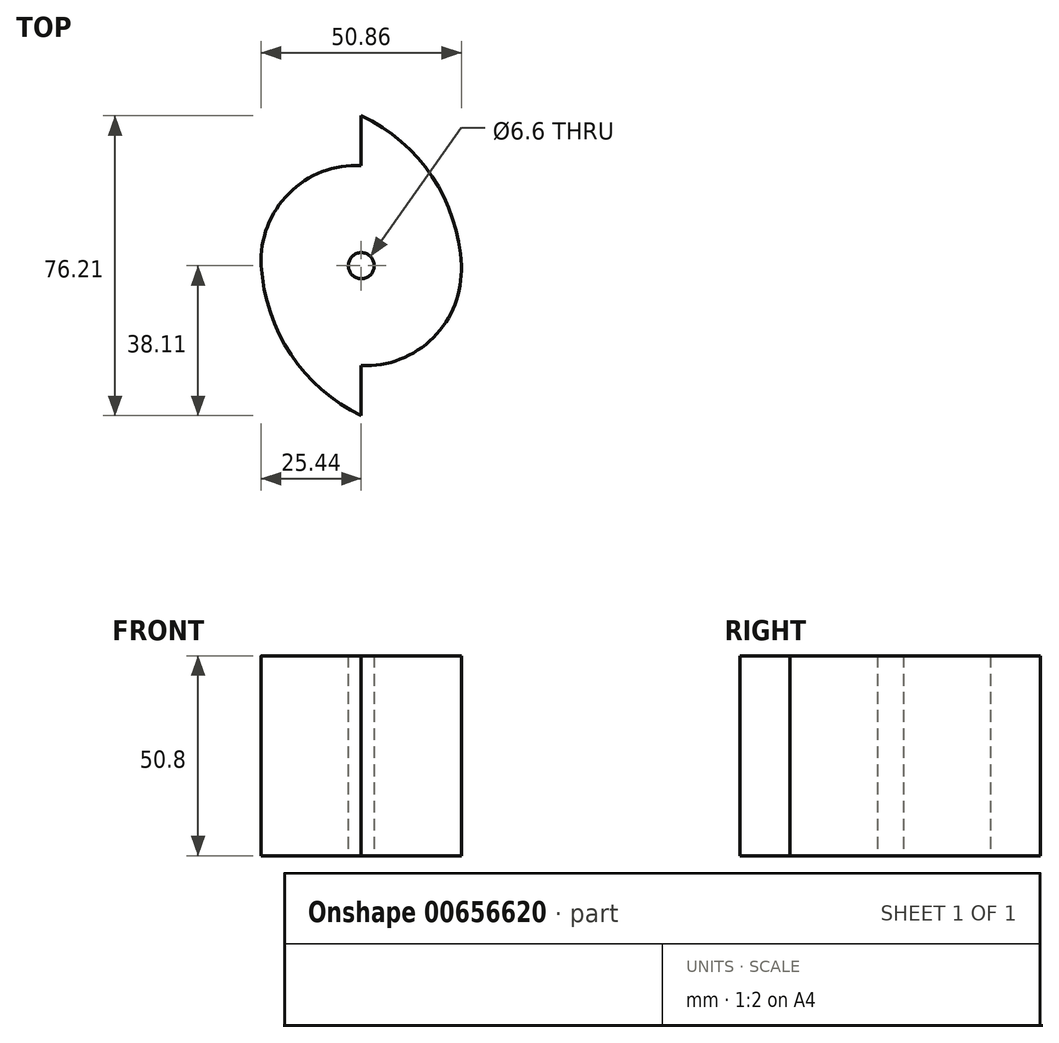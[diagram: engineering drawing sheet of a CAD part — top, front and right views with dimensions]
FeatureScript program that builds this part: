
annotation { "Feature Type Name" : "Feature", "Feature Type Description" : "" }
export const myFeature = defineFeature(function(context is Context, id is Id, definition is map)
    precondition{}
    {
        {
            var Q0;
            Q0=qCreatedBy(makeId("Top.planeOp"),FACE);
            var sketch = newSketch(context, id + "F0", { "sketchPlane" : qUnion([Q0])});
            skCircle(sketch, "E0", {"center": v(0, 0) * mm, "radius": 3.3 * mm});
            skLineSegment(sketch, "E1", {"start": v(0, 25.4) * mm, "end": v(0, 38.1) * mm});
            skLineSegment(sketch, "E2", {"start": v(0, -25.4) * mm, "end": v(0, -38.11) * mm});
            skArc(sketch, "E3", {"start": v(25.4, 0) * mm, "mid": v(18.02, 22.6) * mm, "end": v(0, 38.1) * mm});
            skArc(sketch, "E4", {"start": v(-25.4, 0) * mm, "mid": v(-17.89, -22.51) * mm, "end": v(0, -38.11) * mm});
            skArc(sketch, "E5", {"start": v(-25.4, 0) * mm, "mid": v(-18.39, 18.39) * mm, "end": v(0, 25.4) * mm});
            skArc(sketch, "E6", {"start": v(25.4, 0) * mm, "mid": v(18.28, -18.28) * mm, "end": v(0, -25.4) * mm});
            skSolve(sketch);
        }
        {
            var Q0;
            Q0=qSketchRegion(id+"F0",true);
            extrude(context, id + "F1", {"entities" : qUnion([Q0]), "depth" : 50.8 * mm, "offsetDistance" : 25.4 * mm});
        }
    });
